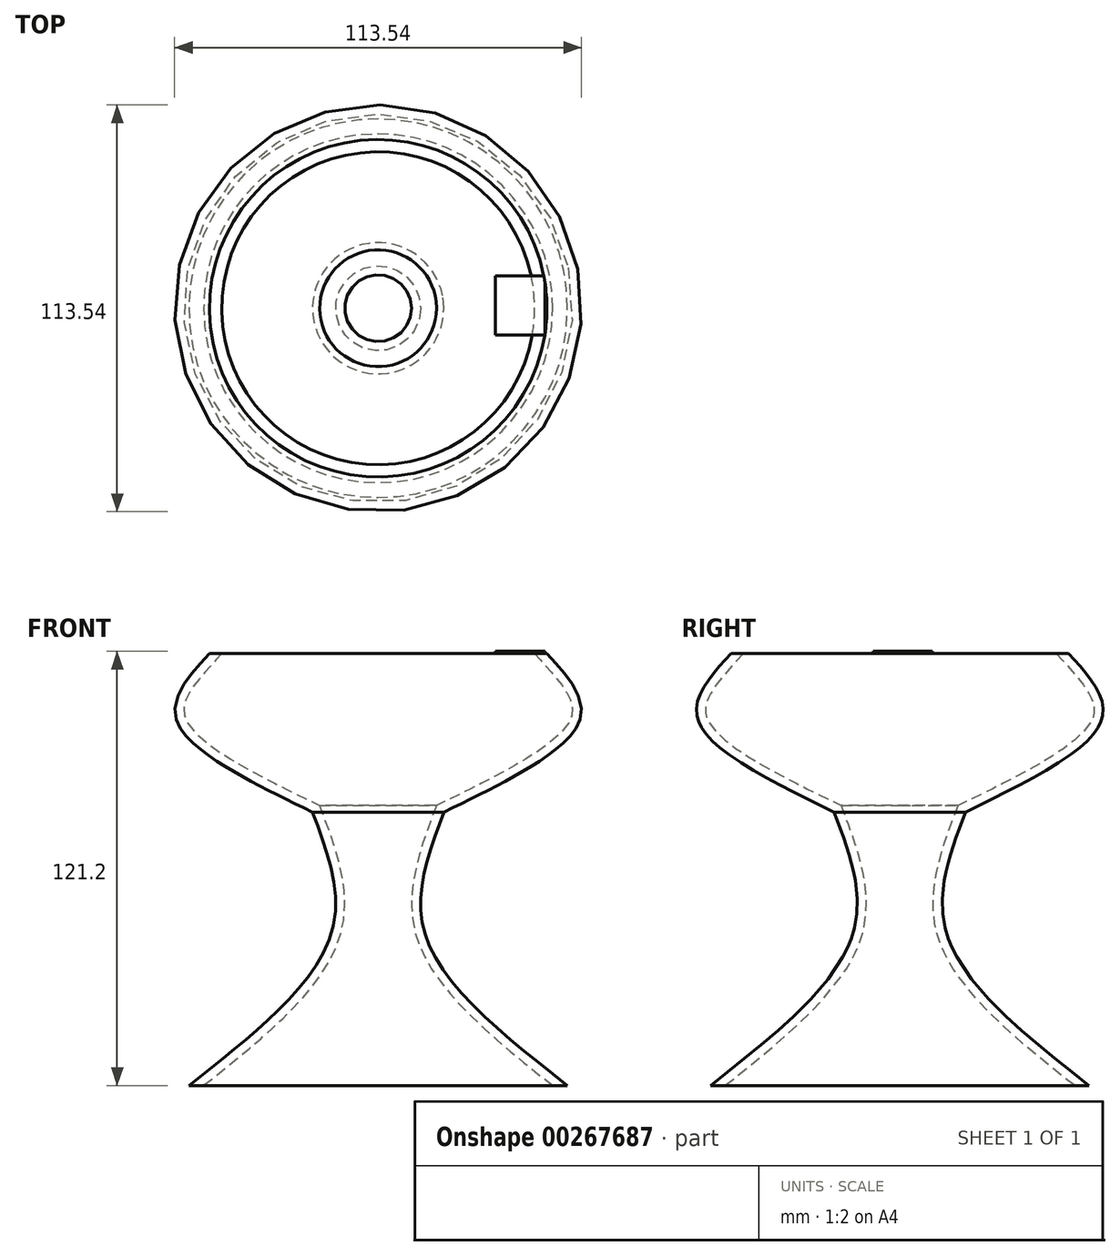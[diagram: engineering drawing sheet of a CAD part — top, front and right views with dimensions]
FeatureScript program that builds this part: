
annotation { "Feature Type Name" : "Feature", "Feature Type Description" : "" }
export const myFeature = defineFeature(function(context is Context, id is Id, definition is map)
    precondition{}
    {
        {
            var Q0;
            Q0=qCreatedBy(makeId("Front.planeOp"),FACE);
            var sketch = newSketch(context, id + "F0", { "sketchPlane" : qUnion([Q0])});
            skFitSpline(sketch, "E0", {"points": [v(-18.31, 0) * mm, v(-13.13, -34.19) * mm, v(-52.81, -76.32) * mm], "startDerivative": vector(29.83, -79.23) * mm, "endDerivative": vector(-93.56, -73.64) * mm});
            skFitSpline(sketch, "E1", {"points": [v(-18.31, 0) * mm, v(-56.54, 26.46) * mm, v(-47.1, 44.25) * mm], "startDerivative": vector(-89.66, 43.6) * mm, "endDerivative": vector(41.08, 45) * mm});
            skLineSegment(sketch, "E2", {"start": v(-47.1, 44.25) * mm, "end": v(0, 44.25) * mm});
            skLineSegment(sketch, "E3", {"start": v(0, 44.25) * mm, "end": v(0, -76.09) * mm});
            skLineSegment(sketch, "E4", {"start": v(0, -76.09) * mm, "end": v(-52.81, -76.32) * mm});
            skSolve(sketch);
        }
        {
            var Q0;
            Q0=makeQuery(id+"F0.imprint","IMPRINT",FACE,{"disambiguationData":[TD([[makeQuery(id+"F0.imprint","IMPRINT",EDGE,{"derivedFrom":sQuery(id+"F0.wireOp",EDGE,"E0")}),1.0]])]});
            var Q1;
            Q1=sQuery(id+"F0.wireOp",EDGE,"E3");
            revolve(context, id + "F1", {"entities" : qUnion([Q0]), "axis" : qUnion([Q1]), "revolveType" : RevolveType.FULL});
        }
        {
            var Q0;
            Q0=makeQuery(id+"F1.opRevolve","SWEPT_FACE",FACE,{"disambiguationData":[OSD([sQuery(id+"F0.wireOp",EDGE,"E2")])]});
            var Q1;
            Q1=makeQuery(id+"F1.opRevolve","SWEPT_FACE",FACE,{"disambiguationData":[OSD([sQuery(id+"F0.wireOp",EDGE,"E4")])]});
            shell(context, id + "F2", {"entities" : qUnion([Q0, Q1]), "thickness" : 2.54 * mm});
        }
        {
            var Q0;
            Q0=makeQuery(id+"F1.opRevolve","SWEPT_FACE",FACE,{"disambiguationData":[OSD([sQuery(id+"F0.wireOp",EDGE,"E2")])]});
            var sketch = newSketch(context, id + "F3", { "sketchPlane" : qUnion([Q0])});
            skLineSegment(sketch, "E5.bottom", {"start": v(46.5, -7.46) * mm, "end": v(32.74, -7.46) * mm});
            skLineSegment(sketch, "E5.top", {"start": v(46.5, 9.1) * mm, "end": v(32.74, 9.1) * mm});
            skLineSegment(sketch, "E5.left", {"start": v(46.5, -7.46) * mm, "end": v(46.5, 9.1) * mm});
            skLineSegment(sketch, "E5.right", {"start": v(32.74, -7.46) * mm, "end": v(32.74, 9.1) * mm});
            skSolve(sketch);
        }
        {
            var Q0;
            {var subQ0=sQuery(id+"F3.wireOp",EDGE,"E5.right");Q0=makeQuery(id+"F3.imprint","IMPRINT",FACE,{"disambiguationData":[TD([[makeQuery(id+"F3.imprint","IMPRINT",EDGE,{"derivedFrom":subQ0}),-1.0]])]});}
            var Q1;
            {var subQ2=sQuery(id+"F0.wireOp",EDGE,"E2");var subQ3=sQuery(id+"F0.wireOp",EDGE,"E1");var subQ4=makeQuery(id+"F1.opRevolve","SWEPT_EDGE",EDGE,{"disambiguationData":[OSD([subQ3,subQ2])]});var subQ7=sQuery(id+"F3.wireOp",EDGE,"E5.top");var subQ8=makeQuery(id+"F3.imprint","INTERSECT",VERTEX,{"derivedFrom":[subQ4,subQ7]});Q1=makeQuery(id+"F3.imprint","IMPRINT",FACE,{"disambiguationData":[TD([[makeQuery(id+"F3.imprint","IMPRINT",EDGE,{"disambiguationData":[TD([[subQ8,-1.0]])],"derivedFrom":subQ7}),1.0]])]});}
            extrude(context, id + "F4", {"entities" : qUnion([Q0, Q1]), "operationType" : NewBodyOperationType.ADD, "depth" : 0.64 * mm});
        }
    });
